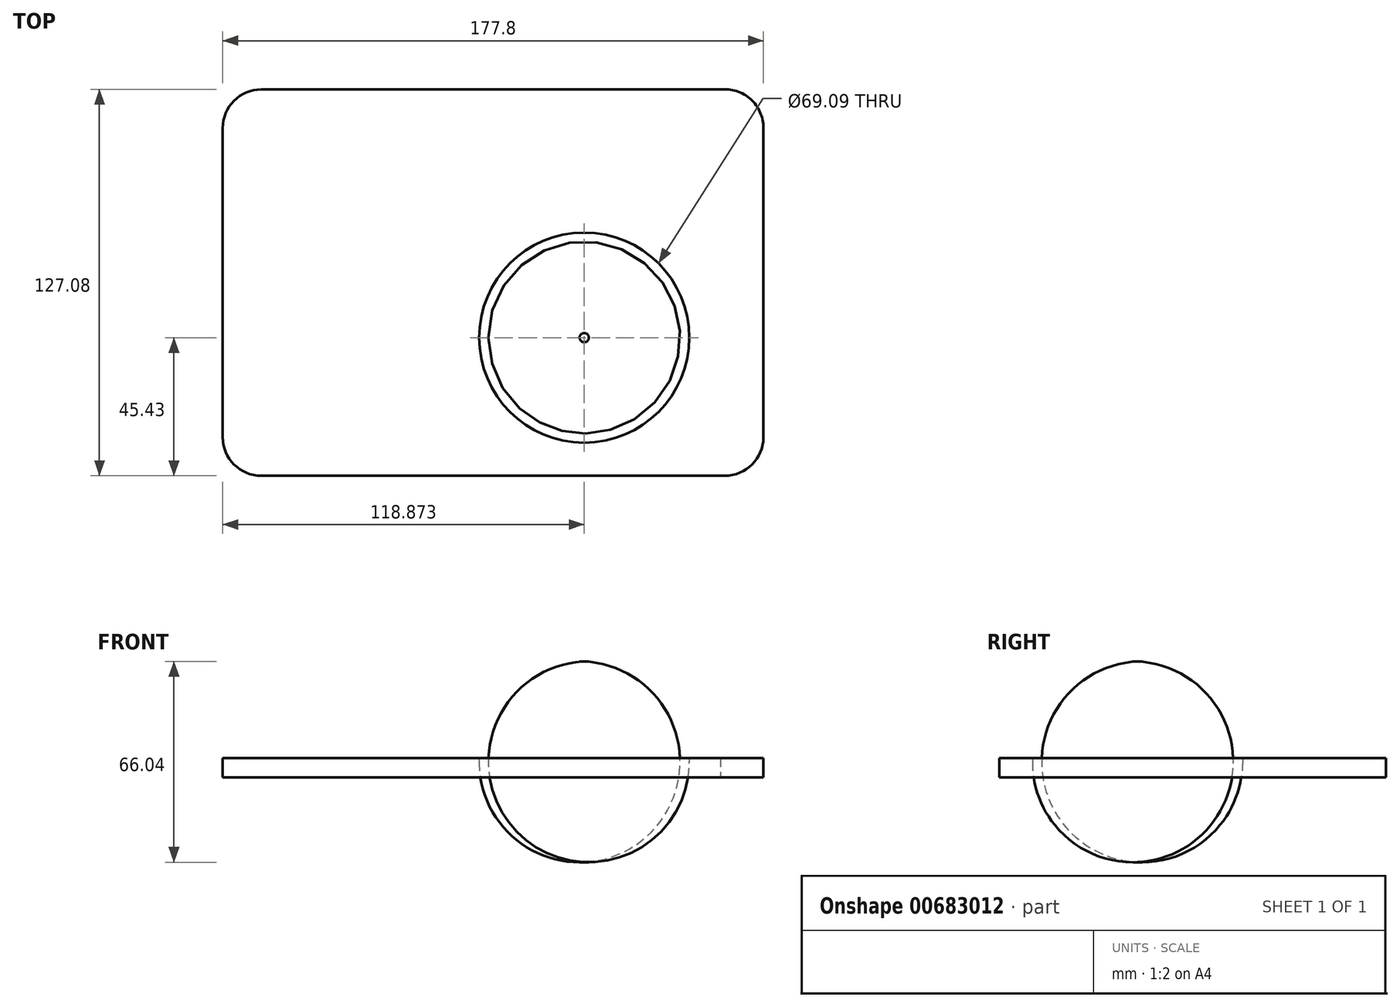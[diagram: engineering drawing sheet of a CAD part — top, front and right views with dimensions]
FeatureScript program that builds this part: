
annotation { "Feature Type Name" : "Feature", "Feature Type Description" : "" }
export const myFeature = defineFeature(function(context is Context, id is Id, definition is map)
    precondition{}
    {
        {
            var Q0;
            Q0=qCreatedBy(makeId("Top.planeOp"),FACE);
            var sketch = newSketch(context, id + "F0", { "sketchPlane" : qUnion([Q0])});
            skLineSegment(sketch, "E0.bottom", {"start": v(76.2, -63.5) * mm, "end": v(-76.2, -63.5) * mm});
            skLineSegment(sketch, "E0.left", {"start": v(88.9, -50.8) * mm, "end": v(88.9, 50.88) * mm});
            skLineSegment(sketch, "E0.right", {"start": v(-88.9, -50.8) * mm, "end": v(-88.9, 50.8) * mm});
            skPoint(sketch, "E0.middle", {"position": v(0, 0) * mm});
            skPoint(sketch, "E1.visualSharp", {"position": v(-88.9, 63.5) * mm});
            skArc(sketch, "E1.filletArc", {"start": v(-76.2, 63.5) * mm, "mid": v(-85.18, 59.78) * mm, "end": v(-88.9, 50.8) * mm});
            skPoint(sketch, "E2.visualSharp", {"position": v(-88.9, -63.5) * mm});
            skArc(sketch, "E2.filletArc", {"start": v(-88.9, -50.8) * mm, "mid": v(-85.18, -59.78) * mm, "end": v(-76.2, -63.5) * mm});
            skPoint(sketch, "E3.visualSharp", {"position": v(88.9, -63.5) * mm});
            skArc(sketch, "E3.filletArc", {"start": v(76.2, -63.5) * mm, "mid": v(85.18, -59.78) * mm, "end": v(88.9, -50.8) * mm});
            skPoint(sketch, "E4.visualSharp", {"position": v(88.9, 63.5) * mm});
            skArc(sketch, "E4.filletArc", {"start": v(88.9, 50.88) * mm, "mid": v(84.65, 60.36) * mm, "end": v(74.74, 63.5) * mm});
            skCircle(sketch, "E5", {"center": v(29.97, -18.07) * mm, "radius": 34.54 * mm});
            skLineSegment(sketch, "E6", {"start": v(-76.2, 63.5) * mm, "end": v(-51.82, 63.5) * mm});
            skLineSegment(sketch, "E7", {"start": v(-31.5, 63.5) * mm, "end": v(74.74, 63.5) * mm});
            skLineSegment(sketch, "E8", {"start": v(-51.82, 63.5) * mm, "end": v(-31.5, 63.5) * mm});
            skSolve(sketch);
        }
        {
            var Q0;
            Q0=makeQuery(id+"F0.imprint","IMPRINT",FACE,{"disambiguationData":[TD([[makeQuery(id+"F0.imprint","IMPRINT",EDGE,{"derivedFrom":sQuery(id+"F0.wireOp",EDGE,"E5")}),1.0]])]});
            extrude(context, id + "F1", {"entities" : qUnion([Q0]), "depth" : 38.1 * mm, "offsetDistance" : 25.4 * mm});
        }
        {
            var Q0;
            Q0=makeQuery(id+"F1.opExtrude","CAP_FACE",FACE,{"disambiguationData":[OSD([sQuery(id+"F0.wireOp",EDGE,"E5")])],"isStart":false});
            fillet(context, id + "F2", {"entities" : qUnion([Q0]), "radius" : 33.02 * mm, "tangentPropagation" : true, "allowEdgeOverflow" : false});
        }
        {
            var Q0;
            Q0 = qSketchRegion(id + "F0", true);
            var Q1;
            Q1 = qConstructionFilter(qBodyType(qCreatedBy(id + "F0" ,EDGE), BodyType.WIRE), ConstructionObject.NO);
            extrude(context, id + "F3", {"entities" : qUnion([Q0]), "bodyType" : ToolBodyType.SURFACE, "surfaceEntities" : qUnion([Q1]), "depth" : 25.4 * mm, "offsetDistance" : 25.4 * mm});
        }
        {
            var Q0;
            Q0 = qSketchRegion(id + "F0", true);
            extrude(context, id + "F4", {"entities" : qUnion([Q0]), "operationType" : NewBodyOperationType.ADD, "depth" : 6.35 * mm, "offsetDistance" : 25.4 * mm});
        }
    });
